# Revit family: QF_Franke_CM_module_en
name_source: partatom
category: Specialty Equipment
revit_build: Autodesk Revit 2018 (Build: 20170223_1515(x64)
units: mm (PartAtom-declared; Revit-internal decimal feet)

## family parameters
Always vertical = Yes
Cut with Voids When Loaded = No
OmniClass Number = 23.40.40.00
OmniClass Title = Food Service Equipment and Furnishings
Part Type = Normal
Room Calculation Point = No
Round Connector Dimension = Use Diameter
Shared = No
Work Plane-Based = No

## types (3) — shared parameters
Assembly Code = E1090320
CE Approved = Yes
Conn Conduit = Yes
Cycle = 50 Hz
Cycle Alternative = 60 Hz
Depth Actual = 385 mm  [stored 1.26312 ft]
ETL Approved = Yes
Energy efficiency label = -
Energy loss acc. to DIN 18873 = -
Height Actual = 190 mm
Housing = QF_Plastic, black
Hygiene Approval = HACCP
Installed By = Franke technician or authorized Franke partner company
Keynote = 11 46 23
Length Actual = 175 mm  [stored 0.574147 ft]
Main switch integrated = Yes
Manufacturer = Franke Kaffeemaschinen AG
Max Overcurrent Protection = 10 A
Model = CM-module
Noise emission = < 70 dB (A)
Number of Nutral Conductors = 1
Number of Poles = 1
Number of Protective Conductors = 1
Omniclass Number = 23.40.40.14.14.14
Power consumption = 0 A
Sanitary feature - Detergent dosage = Automatic water and cleaning agent dosing for cleaning via the connected clean master module
Specification by Manufacturer = The CM module is used for the preparation and provision of the ready-to-use cleaning agent solution for cleaning the connected modules.. Installation under the counter.
URL = https://www.franke.com
URL Critical Spares List = https://shop.franke.com
URL Cutsheet = https://www.franke.com
URL Manufacturer = https://www.franke.com
Warranty Duration = 12 Mon.
Watts max. = 45 W
Watts min. = 0 W
Weight = 2.00 kg

## per-type parameters (varying)
| type | Volts max. | Volts min. |
| 220–240 V 1LNPE 50-60 Hz  45 W 10 A - (CH/GB/EU) | 240 V | 220 V |
| 100 V 1LNPE 50-60 Hz  45 W 10 A - (JP) | 100 V | 0 V |
| 100-127 V 1LNPE 50-60 Hz  45 W 10 A - (USA/LATAM) | 127 V | 100 V |

note: [stored X ft] marks values corroborated as IEEE doubles in the binary element streams (Revit-internal decimal feet)
